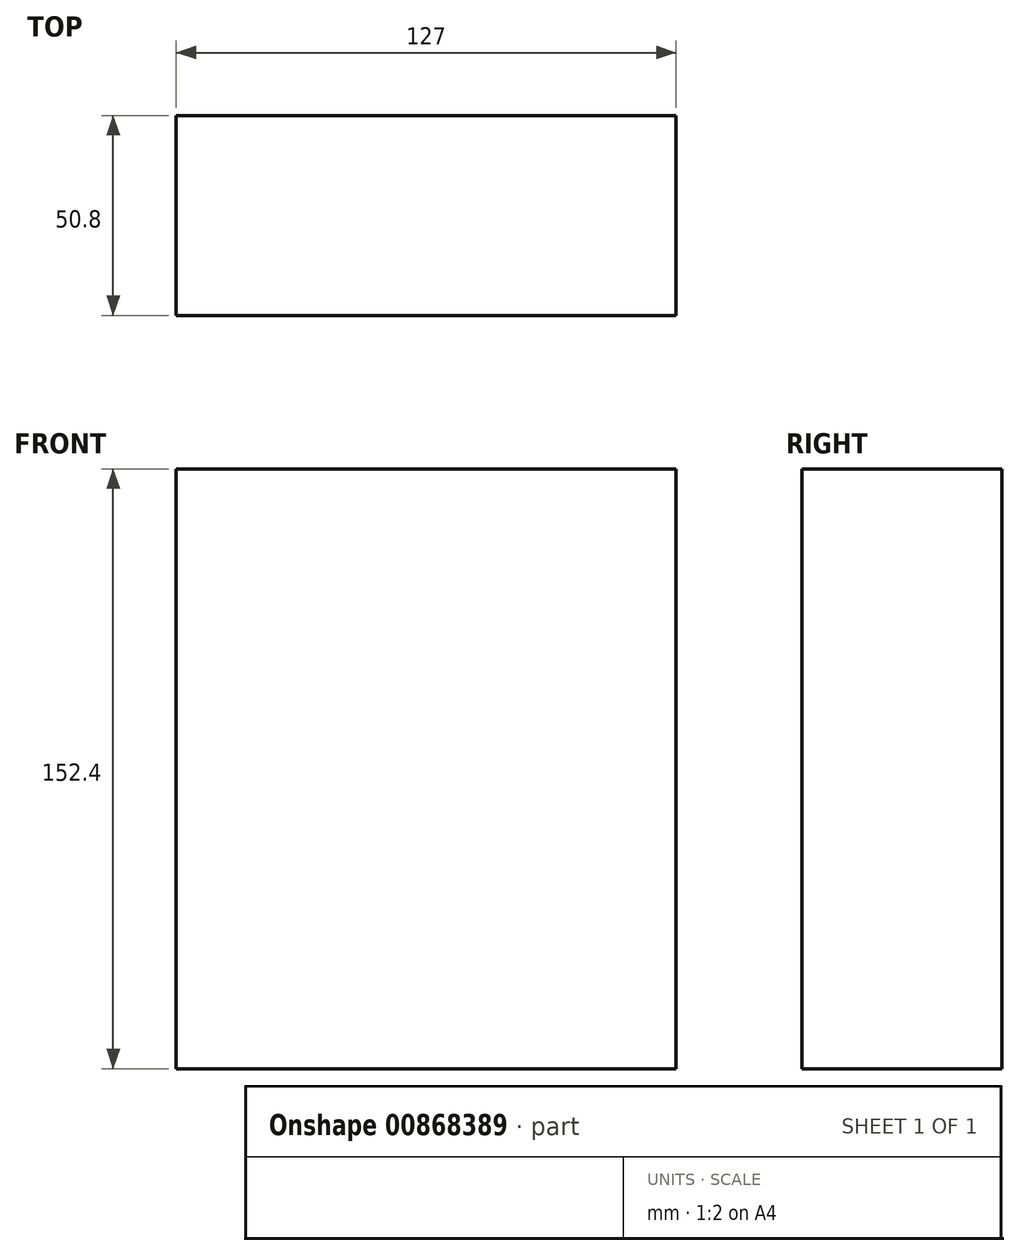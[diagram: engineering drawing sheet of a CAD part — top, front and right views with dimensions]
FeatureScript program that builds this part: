
annotation { "Feature Type Name" : "Feature", "Feature Type Description" : "" }
export const myFeature = defineFeature(function(context is Context, id is Id, definition is map)
    precondition{}
    {
        {
            var Q0;
            Q0=qCreatedBy(makeId("Front.planeOp"),FACE);
            var sketch = newSketch(context, id + "F0", { "sketchPlane" : qUnion([Q0])});
            skLineSegment(sketch, "E0", {"start": v(-63.5, 76.2) * mm, "end": v(63.5, 76.2) * mm});
            skLineSegment(sketch, "E1", {"start": v(63.5, 76.2) * mm, "end": v(63.5, -76.2) * mm});
            skLineSegment(sketch, "E2", {"start": v(63.5, -76.2) * mm, "end": v(-63.5, -76.2) * mm});
            skLineSegment(sketch, "E3", {"start": v(-63.5, -76.2) * mm, "end": v(-63.5, 76.2) * mm});
            skSolve(sketch);
        }
        {
            var Q0;
            Q0 = qSketchRegion(id + "F0", true);
            extrude(context, id + "F1", {"entities" : qUnion([Q0]), "depth" : 25.4 * mm, "offsetDistance" : 25.4 * mm, "hasSecondDirection" : true, "secondDirectionOppositeDirection" : true, "secondDirectionDepth" : 25.4 * mm});
        }
    });
